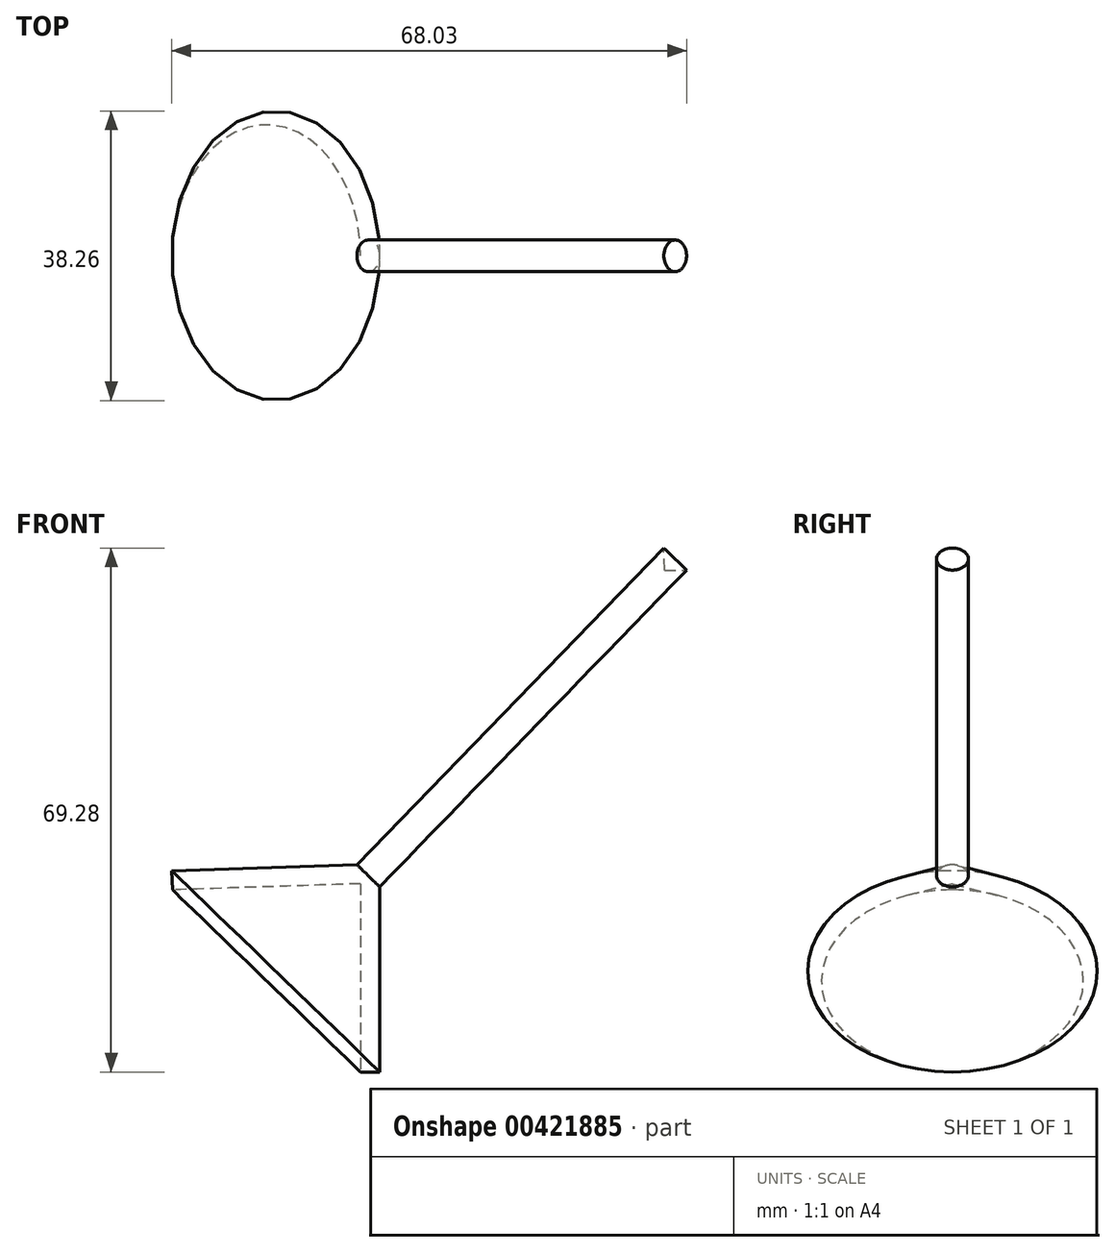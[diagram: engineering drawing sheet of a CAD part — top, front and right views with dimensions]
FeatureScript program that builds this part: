
annotation { "Feature Type Name" : "Feature", "Feature Type Description" : "" }
export const myFeature = defineFeature(function(context is Context, id is Id, definition is map)
    precondition{}
    {
        {
            var Q0;
            Q0=qCreatedBy(makeId("Front.planeOp"),FACE);
            var sketch = newSketch(context, id + "F0", { "sketchPlane" : qUnion([Q0])});
            skLineSegment(sketch, "E0", {"start": v(40.16, 56.14) * mm, "end": v(0, 14.67) * mm});
            skLineSegment(sketch, "E1", {"start": v(0, 14.67) * mm, "end": v(0, -10.22) * mm});
            skLineSegment(sketch, "E2", {"start": v(0, -10.22) * mm, "end": v(2.53, -10.22) * mm});
            skLineSegment(sketch, "E3", {"start": v(2.53, -10.22) * mm, "end": v(2.53, 14.26) * mm});
            skLineSegment(sketch, "E4", {"start": v(2.53, 14.26) * mm, "end": v(43.08, 56.14) * mm});
            skLineSegment(sketch, "E5", {"start": v(43.08, 56.14) * mm, "end": v(40.16, 56.14) * mm});
            skSolve(sketch);
        }
        {
            var Q0;
            Q0=makeQuery(id+"F0.imprint","IMPRINT",FACE,{"disambiguationData":[TD([[makeQuery(id+"F0.imprint","IMPRINT",EDGE,{"derivedFrom":sQuery(id+"F0.wireOp",EDGE,"E0")}),1.0]])]});
            var Q1;
            Q1=sQuery(id+"F0.wireOp",EDGE,"E0");
            revolve(context, id + "F1", {"entities" : qUnion([Q0]), "axis" : qUnion([Q1]), "revolveType" : RevolveType.FULL});
        }
    });
